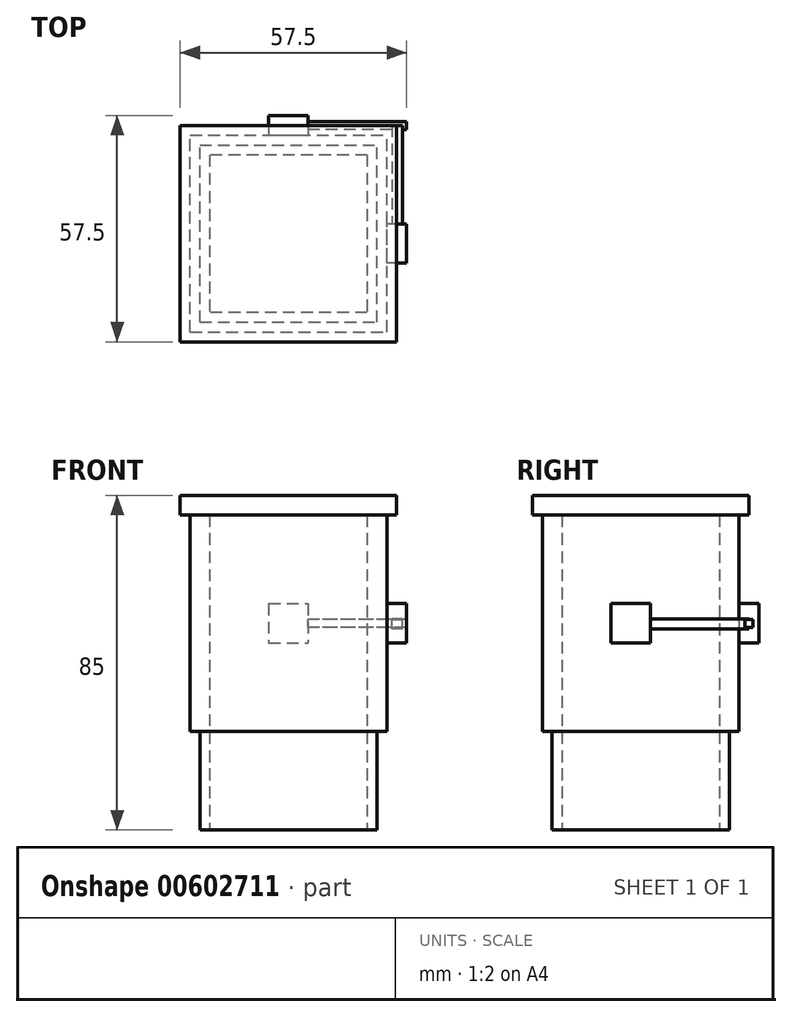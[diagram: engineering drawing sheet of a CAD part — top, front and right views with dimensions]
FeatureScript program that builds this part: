
annotation { "Feature Type Name" : "Feature", "Feature Type Description" : "" }
export const myFeature = defineFeature(function(context is Context, id is Id, definition is map)
    precondition{}
    {
        {
            var Q0;
            Q0=qCreatedBy(makeId("Top.planeOp"),FACE);
            var sketch = newSketch(context, id + "F0", { "sketchPlane" : qUnion([Q0])});
            skLineSegment(sketch, "E0.bottom", {"start": v(0, 0) * mm, "end": v(50, 0) * mm});
            skLineSegment(sketch, "E0.top", {"start": v(0, 50) * mm, "end": v(50, 50) * mm});
            skLineSegment(sketch, "E0.left", {"start": v(0, 0) * mm, "end": v(0, 50) * mm});
            skLineSegment(sketch, "E0.right", {"start": v(50, 0) * mm, "end": v(50, 50) * mm});
            skLineSegment(sketch, "E1.bottom", {"start": v(45, 45) * mm, "end": v(5, 45) * mm});
            skLineSegment(sketch, "E1.top", {"start": v(45, 5) * mm, "end": v(5, 5) * mm});
            skLineSegment(sketch, "E1.left", {"start": v(45, 45) * mm, "end": v(45, 5) * mm});
            skLineSegment(sketch, "E1.right", {"start": v(5, 45) * mm, "end": v(5, 5) * mm});
            skPoint(sketch, "E1.middle", {"position": v(25, 25) * mm});
            skPoint(sketch, "E1.middle.positionSnap0", {"position": v(25, 0) * mm});
            skPoint(sketch, "E1.middle.positionSnap1", {"position": v(50, 25) * mm});
            skPoint(sketch, "E1.centerSnap0", {"position": v(25, 0) * mm});
            skPoint(sketch, "E1.centerSnap1", {"position": v(50, 25) * mm});
            skSolve(sketch);
        }
        {
            var Q0;
            Q0 = qSketchRegion(id + "F0", true);
            extrude(context, id + "F1", {"entities" : qUnion([Q0]), "depth" : 55 * mm, "offsetDistance" : 25 * mm});
        }
        {
            var Q0;
            Q0=makeQuery(id+"F1.opExtrude","CAP_FACE",FACE,{"disambiguationData":[OSD([sQuery(id+"F0.wireOp",EDGE,"E0.bottom"),sQuery(id+"F0.wireOp",EDGE,"E0.top"),sQuery(id+"F0.wireOp",EDGE,"E0.left"),sQuery(id+"F0.wireOp",EDGE,"E0.right"),sQuery(id+"F0.wireOp",EDGE,"E1.bottom"),sQuery(id+"F0.wireOp",EDGE,"E1.top"),sQuery(id+"F0.wireOp",EDGE,"E1.left"),sQuery(id+"F0.wireOp",EDGE,"E1.right")])],"isStart":false});
            var sketch = newSketch(context, id + "F2", { "sketchPlane" : qUnion([Q0])});
            skLineSegment(sketch, "E2.bottom", {"start": v(-2.5, 52.5) * mm, "end": v(52.5, 52.5) * mm});
            skLineSegment(sketch, "E2.top", {"start": v(-2.5, -2.5) * mm, "end": v(52.5, -2.5) * mm});
            skLineSegment(sketch, "E2.left", {"start": v(-2.5, 52.5) * mm, "end": v(-2.5, -2.5) * mm});
            skLineSegment(sketch, "E2.right", {"start": v(52.5, 52.5) * mm, "end": v(52.5, -2.5) * mm});
            skPoint(sketch, "E2.middle", {"position": v(25, 25) * mm});
            skPoint(sketch, "E2.middle.positionSnap0", {"position": v(25, 45) * mm});
            skPoint(sketch, "E2.middle.positionSnap1", {"position": v(5, 25) * mm});
            skPoint(sketch, "E2.centerSnap0", {"position": v(25, 45) * mm});
            skPoint(sketch, "E2.centerSnap1", {"position": v(5, 25) * mm});
            skSolve(sketch);
        }
        {
            var Q0;
            Q0 = qSketchRegion(id + "F2", true);
            extrude(context, id + "F3", {"entities" : qUnion([Q0]), "operationType" : NewBodyOperationType.ADD, "depth" : 5 * mm, "offsetDistance" : 25 * mm});
        }
        {
            var Q0;
            Q0=makeQuery(id+"F1.opExtrude","CAP_FACE",FACE,{"disambiguationData":[OSD([sQuery(id+"F0.wireOp",EDGE,"E0.bottom"),sQuery(id+"F0.wireOp",EDGE,"E0.top"),sQuery(id+"F0.wireOp",EDGE,"E0.left"),sQuery(id+"F0.wireOp",EDGE,"E0.right"),sQuery(id+"F0.wireOp",EDGE,"E1.bottom"),sQuery(id+"F0.wireOp",EDGE,"E1.top"),sQuery(id+"F0.wireOp",EDGE,"E1.left"),sQuery(id+"F0.wireOp",EDGE,"E1.right")])],"isStart":true});
            var sketch = newSketch(context, id + "F4", { "sketchPlane" : qUnion([Q0])});
            skLineSegment(sketch, "E3.bottom", {"start": v(2.5, -2.5) * mm, "end": v(47.5, -2.5) * mm});
            skLineSegment(sketch, "E3.top", {"start": v(2.5, -47.5) * mm, "end": v(47.5, -47.5) * mm});
            skLineSegment(sketch, "E3.left", {"start": v(2.5, -2.5) * mm, "end": v(2.5, -47.5) * mm});
            skLineSegment(sketch, "E3.right", {"start": v(47.5, -2.5) * mm, "end": v(47.5, -47.5) * mm});
            skPoint(sketch, "E3.middle", {"position": v(25, -25) * mm});
            skPoint(sketch, "E3.middle.positionSnap0", {"position": v(25, -5) * mm});
            skPoint(sketch, "E3.middle.positionSnap1", {"position": v(5, -25) * mm});
            skPoint(sketch, "E3.centerSnap0", {"position": v(25, -5) * mm});
            skPoint(sketch, "E3.centerSnap1", {"position": v(5, -25) * mm});
            skLineSegment(sketch, "E4.bottom", {"start": v(45, -5) * mm, "end": v(5, -5) * mm});
            skLineSegment(sketch, "E4.top", {"start": v(45, -45) * mm, "end": v(5, -45) * mm});
            skLineSegment(sketch, "E4.left", {"start": v(45, -5) * mm, "end": v(45, -45) * mm});
            skLineSegment(sketch, "E4.right", {"start": v(5, -5) * mm, "end": v(5, -45) * mm});
            skSolve(sketch);
        }
        {
            var Q0;
            Q0 = qSketchRegion(id + "F4", true);
            extrude(context, id + "F5", {"entities" : qUnion([Q0]), "operationType" : NewBodyOperationType.ADD, "depth" : 25 * mm, "offsetDistance" : 25 * mm});
        }
        {
            var Q0;
            Q0=makeQuery(id+"F1.opExtrude","SWEPT_FACE",FACE,{"disambiguationData":[OSD([sQuery(id+"F0.wireOp",EDGE,"E0.top")])]});
            var sketch = newSketch(context, id + "F6", { "sketchPlane" : qUnion([Q0])});
            skLineSegment(sketch, "E5.bottom", {"start": v(-20, 32.5) * mm, "end": v(-30, 32.5) * mm});
            skLineSegment(sketch, "E5.top", {"start": v(-20, 22.5) * mm, "end": v(-30, 22.5) * mm});
            skLineSegment(sketch, "E5.left", {"start": v(-20, 32.5) * mm, "end": v(-20, 22.5) * mm});
            skLineSegment(sketch, "E5.right", {"start": v(-30, 32.5) * mm, "end": v(-30, 22.5) * mm});
            skPoint(sketch, "E5.middle", {"position": v(-25, 27.5) * mm});
            skPoint(sketch, "E5.middle.positionSnap0", {"position": v(-25, 0) * mm});
            skPoint(sketch, "E5.middle.positionSnap1", {"position": v(0, 27.5) * mm});
            skPoint(sketch, "E5.centerSnap0", {"position": v(-25, 0) * mm});
            skPoint(sketch, "E5.centerSnap1", {"position": v(0, 27.5) * mm});
            skSolve(sketch);
        }
        {
            var Q0;
            Q0 = qSketchRegion(id + "F6", true);
            extrude(context, id + "F7", {"entities" : qUnion([Q0]), "operationType" : NewBodyOperationType.ADD, "depth" : 5 * mm, "offsetDistance" : 25 * mm});
        }
        {
            var Q0;
            Q0=makeQuery(id+"F7.opExtrude","SWEPT_FACE",FACE,{"disambiguationData":[OSD([sQuery(id+"F6.wireOp",EDGE,"E5.right")])]});
            var sketch = newSketch(context, id + "F8", { "sketchPlane" : qUnion([Q0])});
            skLineSegment(sketch, "E6.bottom", {"start": v(53.5, 26.5) * mm, "end": v(51.5, 26.5) * mm});
            skLineSegment(sketch, "E6.top", {"start": v(53.5, 28.5) * mm, "end": v(51.5, 28.5) * mm});
            skLineSegment(sketch, "E6.left", {"start": v(53.5, 26.5) * mm, "end": v(53.5, 28.5) * mm});
            skLineSegment(sketch, "E6.right", {"start": v(51.5, 26.5) * mm, "end": v(51.5, 28.5) * mm});
            skPoint(sketch, "E6.middle", {"position": v(52.5, 27.5) * mm});
            skPoint(sketch, "E6.middle.positionSnap0", {"position": v(52.5, 22.5) * mm});
            skPoint(sketch, "E6.middle.positionSnap1", {"position": v(50, 27.5) * mm});
            skPoint(sketch, "E6.centerSnap0", {"position": v(52.5, 22.5) * mm});
            skPoint(sketch, "E6.centerSnap1", {"position": v(50, 27.5) * mm});
            skSolve(sketch);
        }
        {
            var Q0;
            Q0 = qSketchRegion(id + "F8", true);
            extrude(context, id + "F9", {"entities" : qUnion([Q0]), "operationType" : NewBodyOperationType.ADD, "depth" : 25 * mm, "offsetDistance" : 25 * mm});
        }
        {
            var Q0;
            Q0=makeQuery(id+"F1.opExtrude","SWEPT_FACE",FACE,{"disambiguationData":[OSD([sQuery(id+"F0.wireOp",EDGE,"E0.right")])]});
            var sketch = newSketch(context, id + "F10", { "sketchPlane" : qUnion([Q0])});
            skSolve(sketch);
        }
        {
            var Q0;
            {var subQ0=sQuery(id+"F0.wireOp",EDGE,"E0.right");Q0=makeQuery(id+"F10.imprint","IMPRINT",FACE,{"disambiguationData":[TD([[makeQuery(id+"F10.imprint","IMPRINT",EDGE,{"derivedFrom":makeQuery(id+"F1.opExtrude","CAP_EDGE",EDGE,{"disambiguationData":[OSD([subQ0])],"isStart":true})}),1.0]])]});}
            var sketch = newSketch(context, id + "F11", { "sketchPlane" : qUnion([Q0])});
            skLineSegment(sketch, "E7.bottom", {"start": v(17.5, 32.5) * mm, "end": v(27.5, 32.5) * mm});
            skLineSegment(sketch, "E7.top", {"start": v(17.5, 22.5) * mm, "end": v(27.5, 22.5) * mm});
            skLineSegment(sketch, "E7.left", {"start": v(17.5, 32.5) * mm, "end": v(17.5, 22.5) * mm});
            skLineSegment(sketch, "E7.right", {"start": v(27.5, 32.5) * mm, "end": v(27.5, 22.5) * mm});
            skPoint(sketch, "E7.middle", {"position": v(22.5, 27.5) * mm});
            skSolve(sketch);
        }
        {
            var Q0;
            Q0 = qSketchRegion(id + "F11", true);
            extrude(context, id + "F12", {"entities" : qUnion([Q0]), "operationType" : NewBodyOperationType.ADD, "depth" : 5 * mm, "offsetDistance" : 25 * mm});
        }
        {
            var Q0;
            Q0=makeQuery(id+"F12.opExtrude","SWEPT_FACE",FACE,{"disambiguationData":[OSD([sQuery(id+"F11.wireOp",EDGE,"E7.right")])]});
            var sketch = newSketch(context, id + "F13", { "sketchPlane" : qUnion([Q0])});
            skLineSegment(sketch, "E8.bottom", {"start": v(-54.02, 26.09) * mm, "end": v(-51.27, 26.09) * mm});
            skLineSegment(sketch, "E8.top", {"start": v(-54.02, 28.66) * mm, "end": v(-51.27, 28.66) * mm});
            skLineSegment(sketch, "E8.left", {"start": v(-54.02, 26.09) * mm, "end": v(-54.02, 28.66) * mm});
            skLineSegment(sketch, "E8.right", {"start": v(-51.27, 26.09) * mm, "end": v(-51.27, 28.66) * mm});
            skPoint(sketch, "E8.middle", {"position": v(-52.65, 27.37) * mm});
            skSolve(sketch);
        }
        {
            var Q0;
            Q0 = qSketchRegion(id + "F13", true);
            extrude(context, id + "F14", {"entities" : qUnion([Q0]), "operationType" : NewBodyOperationType.ADD, "depth" : 25 * mm, "offsetDistance" : 25 * mm});
        }
    });
